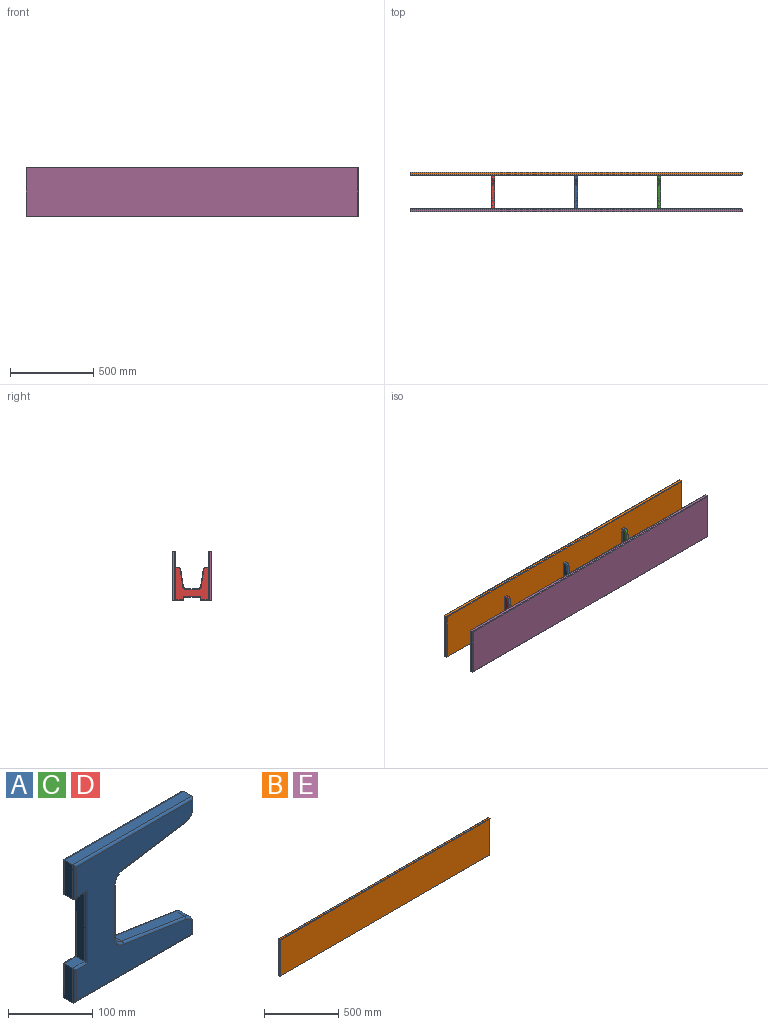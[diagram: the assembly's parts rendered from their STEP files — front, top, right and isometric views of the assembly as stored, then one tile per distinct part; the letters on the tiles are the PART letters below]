
ASSEMBLY  parts=5 mates=4
PART A: 50 faces, bbox 201.2x20x200 mm
  f0: plane 74.26x14mm, normal (1,0,0), area 1039.7mm2, adj f1,f15,f29,f45
  f1: cylinder r=15mm len=14.83mm, axis (0,1,0), area 297.8mm2, adj f0,f2,f27,f43
  f2: plane 104.56x16.09mm, normal (0.15,0,-0.99), area 1481.1mm2, adj f1,f3,f25,f41
  f3: cylinder r=15mm len=14.83mm, axis (0,1,0), area 297.8mm2, adj f2,f4,f23,f39
  f4: plane 17.13x14mm, normal (1,0,0), area 239.8mm2, adj f3,f5,f21,f37
  f5: plane 200x14mm, normal (0,0,1), area 2800mm2, adj f4,f6,f19,f35
  f6: plane 50x14mm, normal (-1,0,0), area 700mm2, adj f5,f7,f18,f34
  f7: plane 20x14mm, normal (0,0,-1), area 280mm2, adj f6,f8,f20,f36
  f8: plane 100x14mm, normal (-1,0,0), area 1400mm2, adj f7,f9,f22,f38
  f9: plane 20x14mm, normal (0,0,1), area 280mm2, adj f8,f10,f24,f40
  f10: plane 50x14mm, normal (-1,0,0), area 700mm2, adj f9,f11,f26,f42
  f11: plane 200x14mm, normal (0,0,-1), area 2800mm2, adj f10,f12,f28,f44
  f12: plane 17.13x14mm, normal (1,0,0), area 239.8mm2, adj f11,f13,f30,f46
  f13: cylinder r=15mm len=14.83mm, axis (0,1,0), area 297.8mm2, adj f12,f14,f32,f48
  f14: plane 104.56x16.09mm, normal (0.15,0,0.99), area 1481.1mm2, adj f13,f15,f33,f49
  f15: cylinder r=15mm len=14.83mm, axis (0,1,0), area 297.8mm2, adj f0,f14,f31,f47
  f16: plane 194x194mm, normal (0,-1,0), area 19300.4mm2, adj f34,f35,f36,f37,f38,f39,f40,f41
  f17: plane 194x194mm, normal (0,1,0), area 19300.4mm2, adj f18,f19,f20,f21,f22,f23,f24,f25
  f18: cylinder r=3mm len=50mm, axis (0,0,-1), area 225.3mm2, adj f6,f17,f19,f20
  f19: cylinder r=3mm len=200mm, axis (-1,0,0), area 932.2mm2, adj f5,f17,f18,f21
  f20: cylinder r=3mm len=23mm, axis (1,0,0), area 94.2mm2, adj f7,f17,f18,f22
  f21: cylinder r=3mm len=17.13mm, axis (0,0,1), area 75.6mm2, adj f4,f17,f19,f23
  f22: cylinder r=3mm len=106mm, axis (0,0,-1), area 481.5mm2, adj f8,f17,f20,f24
  f23: torus R=12mm, axis (0,-1,0), area 93mm2, adj f3,f17,f21,f25
  f24: cylinder r=3mm len=23mm, axis (-1,0,0), area 94.2mm2, adj f9,f17,f22,f26
  f25: cylinder r=3mm len=105.02mm, axis (0.99,0,0.15), area 498.5mm2, adj f2,f17,f23,f27
  f26: cylinder r=3mm len=50mm, axis (0,0,-1), area 225.3mm2, adj f10,f17,f24,f28
  f27: torus R=18mm, axis (0,-1,0), area 107.5mm2, adj f1,f17,f25,f29
  f28: cylinder r=3mm len=200mm, axis (1,0,0), area 932.2mm2, adj f11,f17,f26,f30
  f29: cylinder r=3mm len=74.26mm, axis (0,0,1), area 350mm2, adj f0,f17,f27,f31
  f30: cylinder r=3mm len=17.13mm, axis (0,0,1), area 75.6mm2, adj f12,f17,f28,f32
  f31: torus R=18mm, axis (0,-1,0), area 107.5mm2, adj f15,f17,f29,f33
  f32: torus R=12mm, axis (0,-1,0), area 93mm2, adj f13,f17,f30,f33
  f33: cylinder r=3mm len=105.02mm, axis (-0.99,0,0.15), area 498.5mm2, adj f14,f17,f31,f32
  f34: cylinder r=3mm len=50mm, axis (0,0,1), area 225.3mm2, adj f6,f16,f35,f36
  f35: cylinder r=3mm len=200mm, axis (1,0,0), area 932.2mm2, adj f5,f16,f34,f37
  f36: cylinder r=3mm len=23mm, axis (-1,0,0), area 94.2mm2, adj f7,f16,f34,f38
  f37: cylinder r=3mm len=17.13mm, axis (0,0,-1), area 75.6mm2, adj f4,f16,f35,f39
  f38: cylinder r=3mm len=106mm, axis (0,0,1), area 481.5mm2, adj f8,f16,f36,f40
  f39: torus R=12mm, axis (0,-1,0), area 93mm2, adj f3,f16,f37,f41
  f40: cylinder r=3mm len=23mm, axis (1,0,0), area 94.2mm2, adj f9,f16,f38,f42
  f41: cylinder r=3mm len=105.02mm, axis (-0.99,0,-0.15), area 498.5mm2, adj f2,f16,f39,f43
  f42: cylinder r=3mm len=50mm, axis (0,0,1), area 225.3mm2, adj f10,f16,f40,f44
  f43: torus R=18mm, axis (0,-1,0), area 107.5mm2, adj f1,f16,f41,f45
  f44: cylinder r=3mm len=200mm, axis (-1,0,0), area 932.2mm2, adj f11,f16,f42,f46
  f45: cylinder r=3mm len=74.26mm, axis (0,0,-1), area 350mm2, adj f0,f16,f43,f47
  f46: cylinder r=3mm len=17.13mm, axis (0,0,-1), area 75.6mm2, adj f12,f16,f44,f48
  f47: torus R=18mm, axis (0,-1,0), area 107.5mm2, adj f15,f16,f45,f49
  f48: torus R=12mm, axis (0,-1,0), area 93mm2, adj f13,f16,f46,f49
  f49: cylinder r=3mm len=105.02mm, axis (0.99,0,-0.15), area 498.5mm2, adj f14,f16,f47,f48
PART B: 14 faces, bbox 2000x20x300 mm
  f0: plane 300x14mm, normal (-1,0,0), area 4200mm2, adj f1,f3,f6,f10
  f1: plane 2000x14mm, normal (0,0,-1), area 28000mm2, adj f0,f2,f7,f11
  f2: plane 300x14mm, normal (1,0,0), area 4200mm2, adj f1,f3,f9,f13
  f3: plane 2000x14mm, normal (0,0,1), area 28000mm2, adj f0,f2,f8,f12
  f4: plane 1994x294mm, normal (0,-1,0), area 586236mm2, adj f10,f11,f12,f13
  f5: plane 1994x294mm, normal (0,1,0), area 586236mm2, adj f6,f7,f8,f9
  f6: cylinder r=3mm len=300mm, axis (0,0,-1), area 1403.4mm2, adj f0,f5,f7,f8
  f7: cylinder r=3mm len=2000mm, axis (1,0,0), area 9414.5mm2, adj f1,f5,f6,f9
  f8: cylinder r=3mm len=2000mm, axis (-1,0,0), area 9414.5mm2, adj f3,f5,f6,f9
  f9: cylinder r=3mm len=300mm, axis (0,0,1), area 1403.4mm2, adj f2,f5,f7,f8
  f10: cylinder r=3mm len=300mm, axis (0,0,1), area 1403.4mm2, adj f0,f4,f11,f12
  f11: cylinder r=3mm len=2000mm, axis (-1,0,0), area 9414.5mm2, adj f1,f4,f10,f13
  f12: cylinder r=3mm len=2000mm, axis (1,0,0), area 9414.5mm2, adj f3,f4,f10,f13
  f13: cylinder r=3mm len=300mm, axis (0,0,-1), area 1403.4mm2, adj f2,f4,f11,f12
PART C: same geometry as A
PART D: same geometry as A
PART E: same geometry as B
PLACE A rot(axis=(0.58,-0.58,0.58),120deg) t=(74.26,424.84,102.29)mm
PLACE B rot(axis=(0,0,1),180deg) t=(1084.26,424.84,99.29)mm
PLACE C rot(axis=(-0.58,-0.58,-0.58),120deg) t=(594.26,224.84,102.29)mm
PLACE D rot(axis=(-0.58,-0.58,-0.58),120deg) t=(-405.74,224.84,102.29)mm
PLACE E t=(-915.74,224.84,99.29)mm
MATE fastened A.f5 <-> E.f5  axis (0,-1,0) through (84.26,224.84,192.29)mm
MATE fastened B.f5 <-> C.f5  axis (0,-1,0) through (584.26,424.84,192.29)mm
MATE fastened D.f11 <-> E.f5  axis (0,-1,0) through (-415.74,224.84,192.29)mm
MATE fastened C.f11 <-> E.f5  axis (0,-1,0) through (584.26,224.84,192.29)mm
